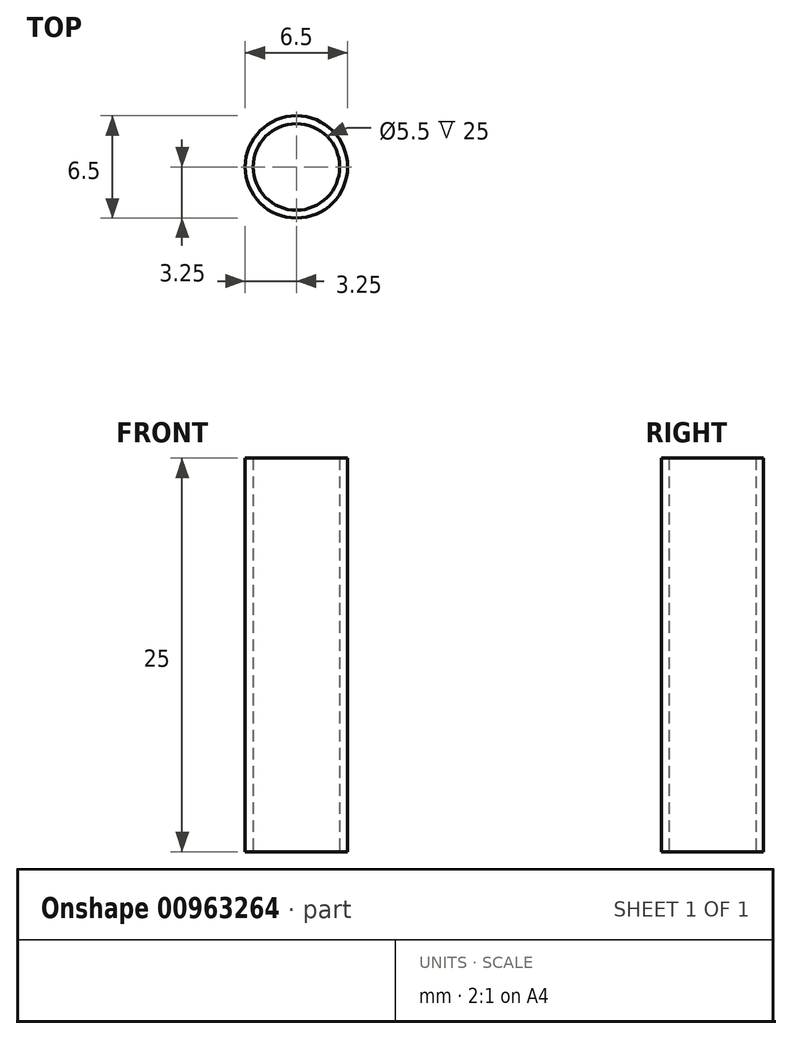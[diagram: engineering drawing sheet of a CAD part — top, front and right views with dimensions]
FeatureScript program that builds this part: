
annotation { "Feature Type Name" : "Feature", "Feature Type Description" : "" }
export const myFeature = defineFeature(function(context is Context, id is Id, definition is map)
    precondition{}
    {
        {
            var Q0;
            Q0=qCreatedBy(makeId("Top.planeOp"),FACE);
            var sketch = newSketch(context, id + "F0", { "sketchPlane" : qUnion([Q0])});
            skCircle(sketch, "E0", {"center": v(0, 0) * mm, "radius": 2.75 * mm});
            skCircle(sketch, "E1", {"center": v(0, 0) * mm, "radius": 3.25 * mm});
            skSolve(sketch);
        }
        {
            var Q0;
            Q0=makeQuery(id+"F0.imprint","IMPRINT",FACE,{"disambiguationData":[TD([[makeQuery(id+"F0.imprint","IMPRINT",EDGE,{"derivedFrom":sQuery(id+"F0.wireOp",EDGE,"E0")}),-1.0]])]});
            extrude(context, id + "F1", {"entities" : qUnion([Q0]), "depth" : 25 * mm, "offsetDistance" : 25 * mm});
        }
    });
